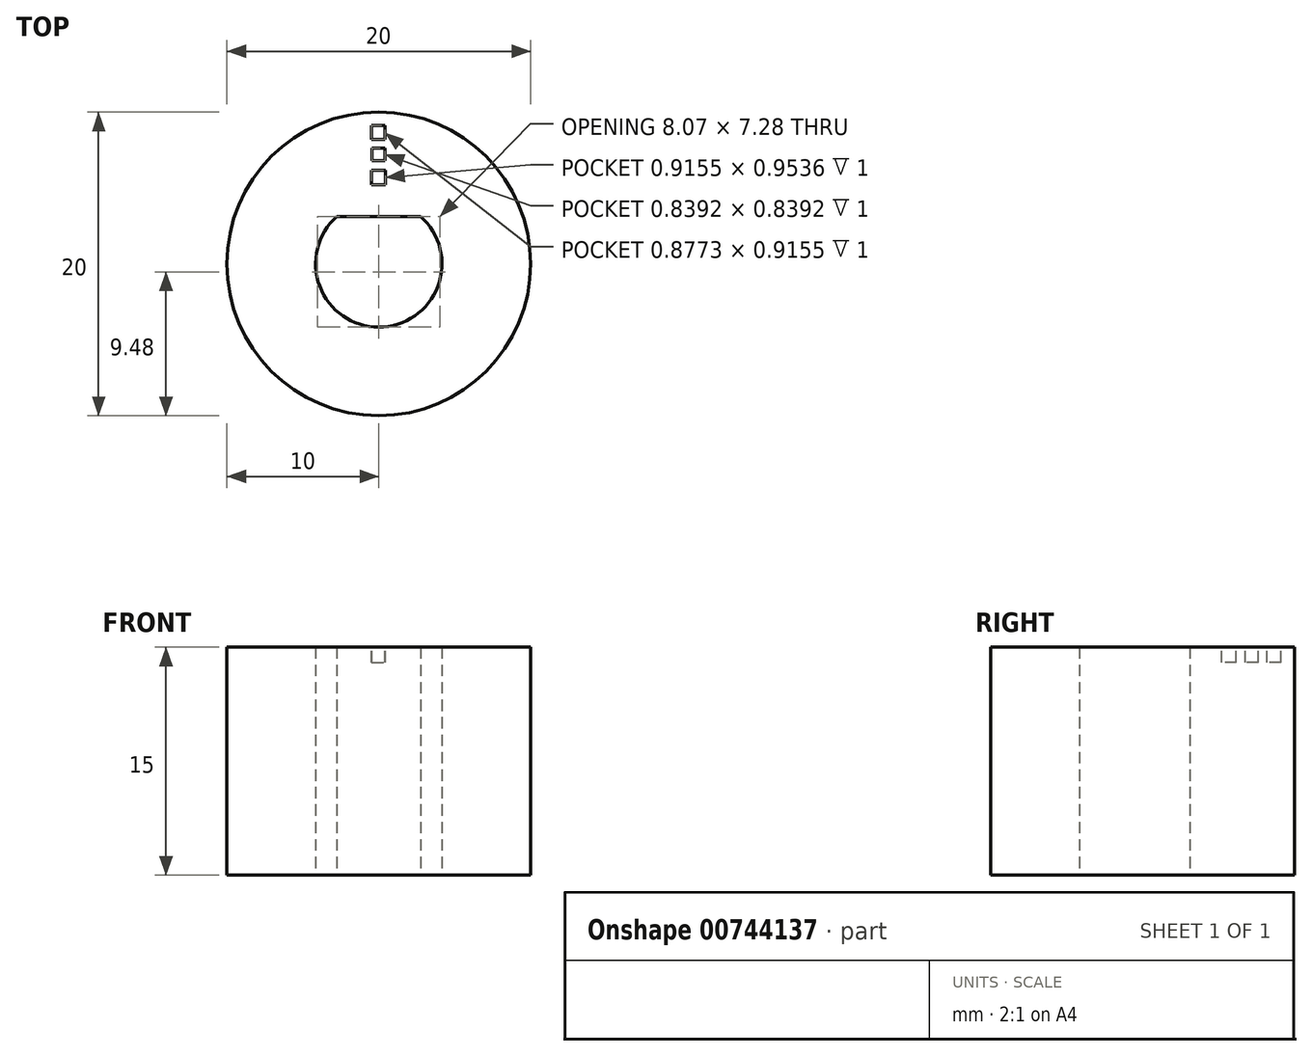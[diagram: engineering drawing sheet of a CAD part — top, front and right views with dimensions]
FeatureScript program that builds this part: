
annotation { "Feature Type Name" : "Feature", "Feature Type Description" : "" }
export const myFeature = defineFeature(function(context is Context, id is Id, definition is map)
    precondition{}
    {
        {
            var Q0;
            Q0=qCreatedBy(makeId("Top.planeOp"),FACE);
            var sketch = newSketch(context, id + "F0", { "sketchPlane" : qUnion([Q0])});
            skCircle(sketch, "E0", {"center": v(0, 0) * mm, "radius": 10 * mm});
            skArc(sketch, "E1", {"start": v(-2.75, 3.12) * mm, "mid": v(0, -4.16) * mm, "end": v(2.75, 3.12) * mm});
            skLineSegment(sketch, "E2", {"start": v(-2.75, 3.12) * mm, "end": v(2.75, 3.12) * mm});
            skSolve(sketch);
        }
        {
            var Q0;
            Q0=makeQuery(id+"F0.imprint","IMPRINT",FACE,{"disambiguationData":[TD([[makeQuery(id+"F0.imprint","IMPRINT",EDGE,{"derivedFrom":sQuery(id+"F0.wireOp",EDGE,"E0")}),1.0]])]});
            extrude(context, id + "F1", {"entities" : qUnion([Q0]), "depth" : 15 * mm, "offsetDistance" : 25 * mm});
        }
        {
            var Q0;
            Q0=makeQuery(id+"F1.opExtrude","CAP_FACE",FACE,{"disambiguationData":[OSD([sQuery(id+"F0.wireOp",EDGE,"E0"),sQuery(id+"F0.wireOp",EDGE,"E1"),sQuery(id+"F0.wireOp",EDGE,"E2")])],"isStart":false});
            var sketch = newSketch(context, id + "F2", { "sketchPlane" : qUnion([Q0])});
            skLineSegment(sketch, "E3.bottom", {"start": v(-0.47, 9.11) * mm, "end": v(0.4, 9.11) * mm});
            skLineSegment(sketch, "E3.top", {"start": v(-0.47, 8.2) * mm, "end": v(0.4, 8.2) * mm});
            skLineSegment(sketch, "E3.left", {"start": v(-0.47, 9.11) * mm, "end": v(-0.47, 8.2) * mm});
            skLineSegment(sketch, "E3.right", {"start": v(0.4, 9.11) * mm, "end": v(0.4, 8.2) * mm});
            skLineSegment(sketch, "E4.bottom", {"start": v(-0.43, 7.62) * mm, "end": v(0.4, 7.62) * mm});
            skLineSegment(sketch, "E4.top", {"start": v(-0.43, 6.78) * mm, "end": v(0.4, 6.78) * mm});
            skLineSegment(sketch, "E4.left", {"start": v(-0.43, 7.62) * mm, "end": v(-0.43, 6.78) * mm});
            skLineSegment(sketch, "E4.right", {"start": v(0.4, 7.62) * mm, "end": v(0.4, 6.78) * mm});
            skLineSegment(sketch, "E5.bottom", {"start": v(-0.47, 6.17) * mm, "end": v(0.44, 6.17) * mm});
            skLineSegment(sketch, "E5.top", {"start": v(-0.47, 5.22) * mm, "end": v(0.44, 5.22) * mm});
            skLineSegment(sketch, "E5.left", {"start": v(-0.47, 6.17) * mm, "end": v(-0.47, 5.22) * mm});
            skLineSegment(sketch, "E5.right", {"start": v(0.44, 6.17) * mm, "end": v(0.44, 5.22) * mm});
            skSolve(sketch);
        }
        {
            var Q0;
            Q0=makeQuery(id+"F2.imprint","IMPRINT",FACE,{"disambiguationData":[TD([[makeQuery(id+"F2.imprint","IMPRINT",EDGE,{"derivedFrom":sQuery(id+"F2.wireOp",EDGE,"E3.bottom")}),-1.0]])]});
            var Q1;
            Q1=makeQuery(id+"F2.imprint","IMPRINT",FACE,{"disambiguationData":[TD([[makeQuery(id+"F2.imprint","IMPRINT",EDGE,{"derivedFrom":sQuery(id+"F2.wireOp",EDGE,"E4.bottom")}),-1.0]])]});
            var Q2;
            Q2=makeQuery(id+"F2.imprint","IMPRINT",FACE,{"disambiguationData":[TD([[makeQuery(id+"F2.imprint","IMPRINT",EDGE,{"derivedFrom":sQuery(id+"F2.wireOp",EDGE,"E5.bottom")}),-1.0]])]});
            extrude(context, id + "F3", {"entities" : qUnion([Q0, Q1, Q2]), "operationType" : NewBodyOperationType.REMOVE, "oppositeDirection" : true, "depth" : 1 * mm, "offsetDistance" : 25 * mm});
        }
    });
